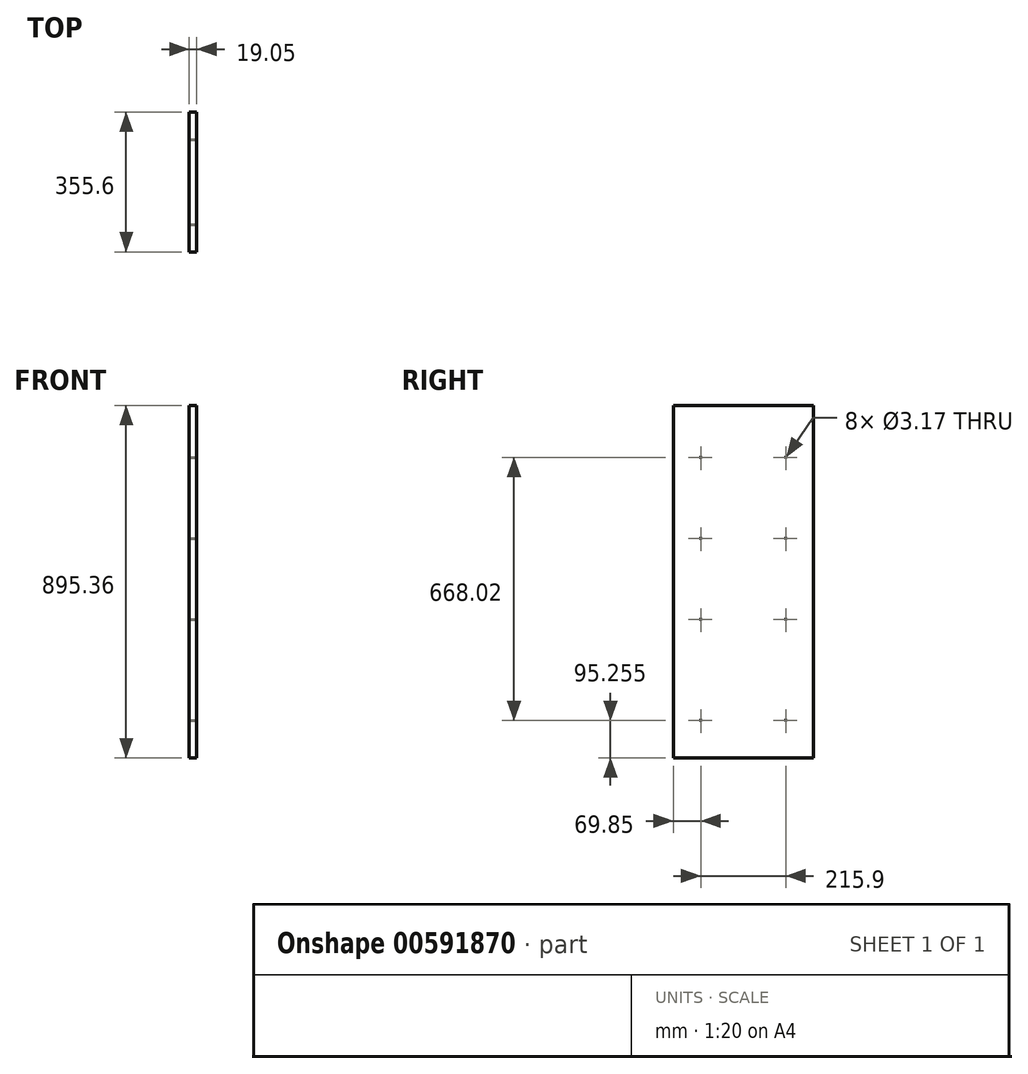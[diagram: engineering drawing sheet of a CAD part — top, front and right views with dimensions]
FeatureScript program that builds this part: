
annotation { "Feature Type Name" : "Feature", "Feature Type Description" : "" }
export const myFeature = defineFeature(function(context is Context, id is Id, definition is map)
    precondition{}
    {
        {
            var Q0;
            Q0=qCreatedBy(makeId("Right.planeOp"),FACE);
            var sketch = newSketch(context, id + "F0", { "sketchPlane" : qUnion([Q0])});
            skLineSegment(sketch, "E0.bottom", {"start": v(177.8, 447.68) * mm, "end": v(-177.8, 447.68) * mm});
            skLineSegment(sketch, "E0.top", {"start": v(177.8, -447.67) * mm, "end": v(-177.8, -447.67) * mm});
            skLineSegment(sketch, "E0.left", {"start": v(177.8, 447.68) * mm, "end": v(177.8, -447.67) * mm});
            skLineSegment(sketch, "E0.right", {"start": v(-177.8, 447.68) * mm, "end": v(-177.8, -447.67) * mm});
            skPoint(sketch, "E0.middle", {"position": v(0, 0) * mm});
            skSolve(sketch);
        }
        {
            var Q0;
            Q0=makeQuery(id+"F0.imprint","IMPRINT",FACE,{"disambiguationData":[TD([[makeQuery(id+"F0.imprint","IMPRINT",EDGE,{"derivedFrom":sQuery(id+"F0.wireOp",EDGE,"E0.bottom")}),1.0]])]});
            extrude(context, id + "F1", {"entities" : qUnion([Q0]), "depth" : 19.05 * mm, "offsetDistance" : 25.4 * mm});
        }
        {
            var Q0;
            Q0=makeQuery(id+"F1.opExtrude","CAP_FACE",FACE,{"disambiguationData":[OSD([sQuery(id+"F0.wireOp",EDGE,"E0.bottom"),sQuery(id+"F0.wireOp",EDGE,"E0.top"),sQuery(id+"F0.wireOp",EDGE,"E0.left"),sQuery(id+"F0.wireOp",EDGE,"E0.right")])],"isStart":false});
            var sketch = newSketch(context, id + "F2", { "sketchPlane" : qUnion([Q0])});
            skLineSegment(sketch, "E1.bottom", {"start": v(-177.8, -447.67) * mm, "end": v(177.8, -447.67) * mm});
            skLineSegment(sketch, "E1.top", {"start": v(-177.8, -428.62) * mm, "end": v(177.8, -428.62) * mm});
            skLineSegment(sketch, "E1.left", {"start": v(-177.8, -447.67) * mm, "end": v(-177.8, -428.62) * mm});
            skLineSegment(sketch, "E1.right", {"start": v(177.8, -447.67) * mm, "end": v(177.8, -428.62) * mm});
            skLineSegment(sketch, "E2", {"start": v(0, -828.68) * mm, "end": v(0, -428.62) * mm});
            skLineSegment(sketch, "E3", {"start": v(-177.8, -352.42) * mm, "end": v(-107.95, -352.42) * mm});
            skLineSegment(sketch, "E4", {"start": v(177.8, -352.42) * mm, "end": v(107.95, -352.42) * mm});
            skLineSegment(sketch, "E5.bottom", {"start": v(-177.8, -428.62) * mm, "end": v(-196.85, -428.62) * mm});
            skLineSegment(sketch, "E5.top", {"start": v(-177.8, -174.62) * mm, "end": v(-196.85, -174.62) * mm});
            skLineSegment(sketch, "E5.left", {"start": v(-177.8, -428.62) * mm, "end": v(-177.8, -174.62) * mm});
            skLineSegment(sketch, "E5.right", {"start": v(-196.85, -428.62) * mm, "end": v(-196.85, -174.62) * mm});
            skLineSegment(sketch, "E6", {"start": v(-196.85, -174.62) * mm, "end": v(-196.85, -172.08) * mm});
            skLineSegment(sketch, "E7.bottom", {"start": v(-196.85, -172.08) * mm, "end": v(-177.8, -172.08) * mm});
            skLineSegment(sketch, "E7.top", {"start": v(-196.85, 31.12) * mm, "end": v(-177.8, 31.12) * mm});
            skLineSegment(sketch, "E7.left", {"start": v(-196.85, -172.08) * mm, "end": v(-196.85, 31.12) * mm});
            skLineSegment(sketch, "E7.right", {"start": v(-177.8, -172.08) * mm, "end": v(-177.8, 31.12) * mm});
            skLineSegment(sketch, "E8", {"start": v(0, -428.62) * mm, "end": v(0, 447.68) * mm});
            skLineSegment(sketch, "E9", {"start": v(-196.85, 31.12) * mm, "end": v(-196.85, 33.66) * mm});
            skLineSegment(sketch, "E10.bottom", {"start": v(-196.85, 33.66) * mm, "end": v(-177.8, 33.66) * mm});
            skLineSegment(sketch, "E10.top", {"start": v(-196.85, 236.86) * mm, "end": v(-177.8, 236.86) * mm});
            skLineSegment(sketch, "E10.left", {"start": v(-196.85, 33.66) * mm, "end": v(-196.85, 236.86) * mm});
            skLineSegment(sketch, "E10.right", {"start": v(-177.8, 33.66) * mm, "end": v(-177.8, 236.86) * mm});
            skLineSegment(sketch, "E11", {"start": v(0, 447.68) * mm, "end": v(-177.8, 447.68) * mm});
            skLineSegment(sketch, "E12", {"start": v(-196.85, 236.86) * mm, "end": v(-196.85, 239.4) * mm});
            skLineSegment(sketch, "E13.bottom", {"start": v(-196.85, 239.4) * mm, "end": v(-177.8, 239.4) * mm});
            skLineSegment(sketch, "E13.top", {"start": v(-196.85, 442.6) * mm, "end": v(-177.8, 442.6) * mm});
            skLineSegment(sketch, "E13.left", {"start": v(-196.85, 239.4) * mm, "end": v(-196.85, 442.6) * mm});
            skLineSegment(sketch, "E13.right", {"start": v(-177.8, 239.4) * mm, "end": v(-177.8, 442.6) * mm});
            skLineSegment(sketch, "E14", {"start": v(-177.8, -172.08) * mm, "end": v(-177.8, -95.88) * mm});
            skLineSegment(sketch, "E15", {"start": v(-177.8, -95.88) * mm, "end": v(-107.95, -95.88) * mm});
            skLineSegment(sketch, "E16", {"start": v(-177.8, 33.66) * mm, "end": v(-177.8, 109.86) * mm});
            skLineSegment(sketch, "E17", {"start": v(-177.8, 109.86) * mm, "end": v(-107.95, 109.86) * mm});
            skLineSegment(sketch, "E18", {"start": v(-177.8, -428.62) * mm, "end": v(-177.8, -352.43) * mm});
            skLineSegment(sketch, "E19", {"start": v(177.8, -428.62) * mm, "end": v(177.8, -352.42) * mm});
            skLineSegment(sketch, "E20", {"start": v(-177.8, 239.4) * mm, "end": v(-177.8, 315.6) * mm});
            skLineSegment(sketch, "E21", {"start": v(-177.8, 315.6) * mm, "end": v(-107.95, 315.6) * mm});
            skLineSegment(sketch, "E22", {"start": v(107.95, -352.42) * mm, "end": v(107.95, -95.88) * mm});
            skLineSegment(sketch, "E23", {"start": v(107.95, -95.88) * mm, "end": v(107.95, 109.86) * mm});
            skLineSegment(sketch, "E24", {"start": v(107.95, 109.86) * mm, "end": v(107.95, 315.6) * mm});
            skPoint(sketch, "E25", {"position": v(-107.95, 315.6) * mm});
            skPoint(sketch, "E26", {"position": v(107.95, 315.6) * mm});
            skPoint(sketch, "E27", {"position": v(107.95, 109.86) * mm});
            skPoint(sketch, "E28", {"position": v(-107.95, 109.86) * mm});
            skPoint(sketch, "E29", {"position": v(-107.95, -95.88) * mm});
            skPoint(sketch, "E30", {"position": v(107.95, -95.88) * mm});
            skPoint(sketch, "E31", {"position": v(-107.95, -352.42) * mm});
            skPoint(sketch, "E32", {"position": v(107.95, -352.42) * mm});
            skSolve(sketch);
        }
        {
            var Q0;
            Q0=sQuery(id+"F2.wireOp",VERTEX,"E25");
            var Q1;
            Q1=sQuery(id+"F2.wireOp",VERTEX,"E26");
            var Q2;
            Q2=sQuery(id+"F2.wireOp",VERTEX,"E27");
            var Q3;
            Q3=sQuery(id+"F2.wireOp",VERTEX,"E28");
            var Q4;
            Q4=sQuery(id+"F2.wireOp",VERTEX,"E29");
            var Q5;
            Q5=sQuery(id+"F2.wireOp",VERTEX,"E30");
            var Q6;
            Q6=sQuery(id+"F2.wireOp",VERTEX,"E32");
            var Q7;
            Q7=sQuery(id+"F2.wireOp",VERTEX,"E31");
            var Q8;
            Q8=makeQuery(id+"F1.opExtrude","SWEPT_BODY",BODY,{"disambiguationData":[OSD([sQuery(id+"F0.wireOp",EDGE,"E0.bottom"),sQuery(id+"F0.wireOp",EDGE,"E0.top"),sQuery(id+"F0.wireOp",EDGE,"E0.left"),sQuery(id+"F0.wireOp",EDGE,"E0.right")])]});
            hole(context, id + "F3", {"style" : HoleStyle.SIMPLE, "endStyle" : HoleEndStyle.BLIND, "holeDiameter" : 3.17 * mm, "majorDiameter" : 6.35 * mm, "holeDepth" : 14.22 * mm, "isTappedThrough" : true, "tappedDepth" : 12.7 * mm, "tapClearance" : 3, "startFromSketch" : true, "locations" : qUnion([Q0, Q1, Q2, Q3, Q4, Q5, Q6, Q7]), "scope" : qUnion([Q8])});
        }
    });
